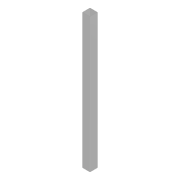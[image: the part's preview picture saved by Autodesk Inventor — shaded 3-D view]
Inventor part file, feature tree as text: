
AUTODESK INVENTOR PART (.ipt)
format: ipt  version: 2020.3 (Build 243373000, 373)  size: 88,064 bytes
history: native  units: mm
features: other x1, extrude x1, sketch x1
ambient origin geometry x8: Origin, YZ Plane, XZ Plane, XY Plane, X Axis, Y Axis, Z Axis, Center Point
bodies: Body1 (feature_tree)
feature tree (3):
  other  "Sólido1"
  extrude  "Extrusão1"  Depth=40.0mm
  sketch  "Esboço1"  dims[d0=40.0mm d1=40.0mm d2=1.5mm d3=1.5mm d4=700.0mm d5=0.0mm]
